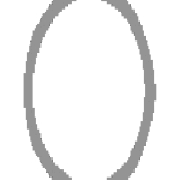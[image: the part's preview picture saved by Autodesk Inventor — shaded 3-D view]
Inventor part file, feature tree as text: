
AUTODESK INVENTOR PART (.ipt)
format: ipt  version: 2021 (Build 250183000, 183)  size: 110,080 bytes
history: native  units: in
note: dims shown in document units (in); Inventor stores cm internally (conversion verified against a paired STEP export)
features: other x4, sketch x3, plane x1
ambient origin geometry x8: Origin, YZ Plane, XZ Plane, XY Plane, X Axis, Y Axis, Z Axis, Center Point
bodies: Solid1 (feature_tree), Body (feature_tree)
feature tree (8):
  other  "Driven Length"
  other  "Frame Generator"
  other  "Start Plane"
  other  "End Plane"
  sketch  "Sketch"  dims[d2=20.5in d4=-0.0in d5=20.5in d6=0.12in d7=0.0in d8=90.0deg d9=20.5in]
  sketch  "Sketch2"  dims[d0=1.0in]
  plane  "Work Plane3"
  sketch  "Sketch3"  dims[d1=0.065in]
